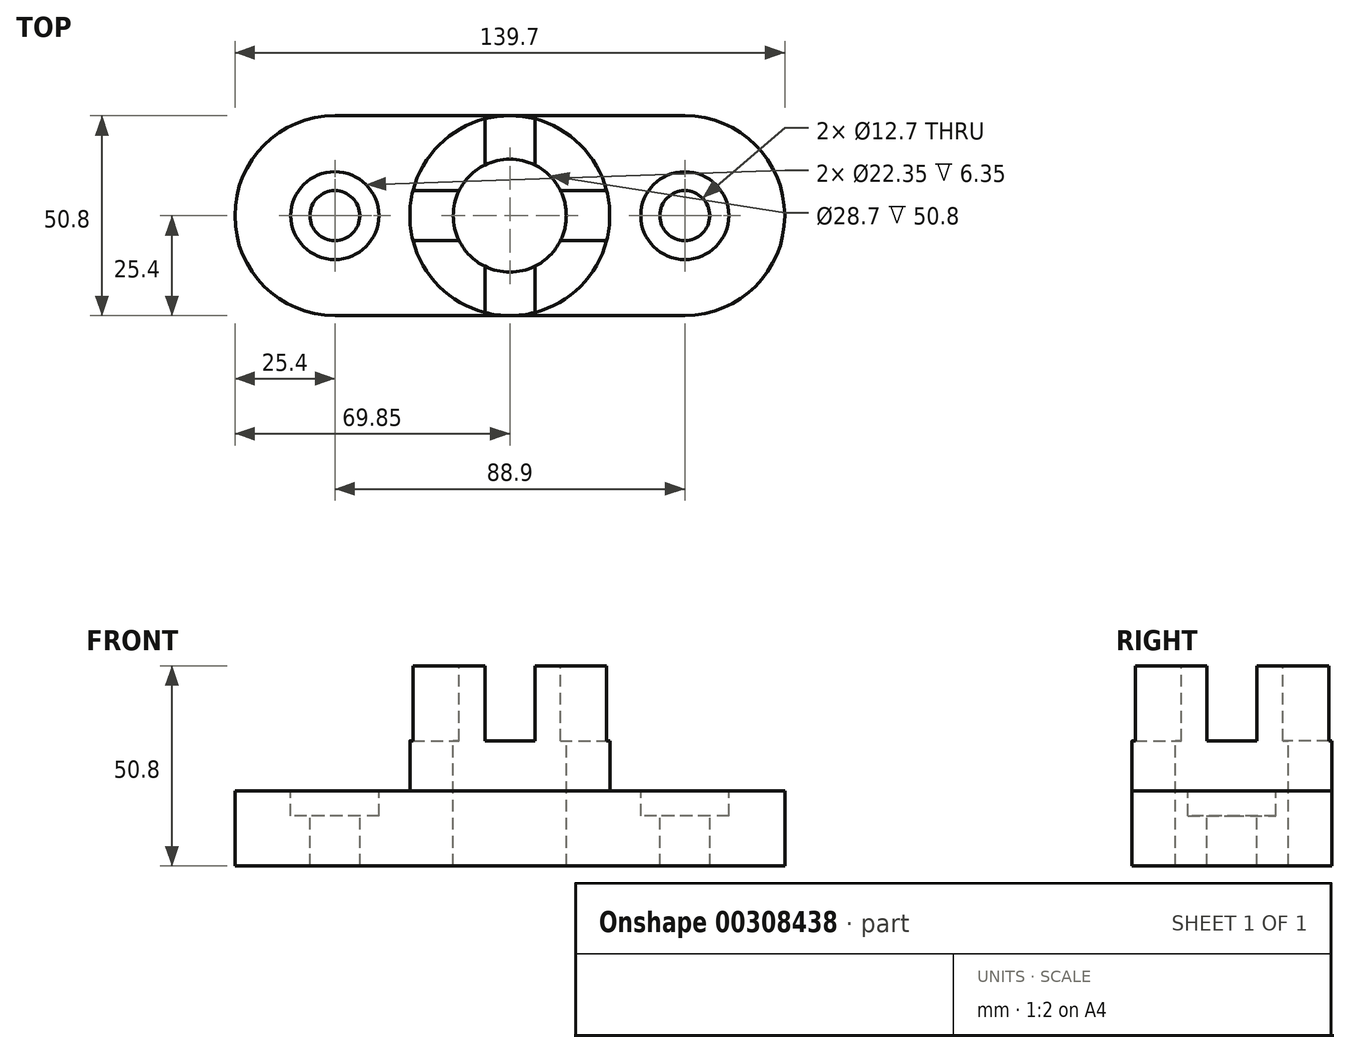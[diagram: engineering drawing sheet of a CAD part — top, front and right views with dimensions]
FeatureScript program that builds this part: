
annotation { "Feature Type Name" : "Feature", "Feature Type Description" : "" }
export const myFeature = defineFeature(function(context is Context, id is Id, definition is map)
    precondition{}
    {
        {
            var Q0;
            Q0=qCreatedBy(makeId("Top.planeOp"),FACE);
            var sketch = newSketch(context, id + "F0", { "sketchPlane" : qUnion([Q0])});
            skLineSegment(sketch, "E0", {"start": v(-44.45, 0) * mm, "end": v(44.45, 0) * mm});
            skLineSegment(sketch, "E1", {"start": v(-44.45, 0) * mm, "end": v(-44.45, 50.8) * mm, "construction": true});
            skLineSegment(sketch, "E2", {"start": v(0, 0) * mm, "end": v(0, 44.45) * mm, "construction": true});
            skArc(sketch, "E3", {"start": v(-44.45, 50.8) * mm, "mid": v(-69.85, 25.4) * mm, "end": v(-44.45, 0) * mm});
            skLineSegment(sketch, "E4.MirrorCS", {"start": v(44.45, 0) * mm, "end": v(44.45, 50.8) * mm, "construction": true});
            skArc(sketch, "E5.MirrorCS", {"start": v(44.45, 50.8) * mm, "mid": v(69.85, 25.4) * mm, "end": v(44.45, 0) * mm});
            skLineSegment(sketch, "E6", {"start": v(-44.45, 50.8) * mm, "end": v(44.45, 50.8) * mm});
            skSolve(sketch);
        }
        {
            var Q0;
            Q0 = qSketchRegion(id + "F0", true);
            extrude(context, id + "F1", {"entities" : qUnion([Q0]), "depth" : 19.05 * mm});
        }
        {
            var Q0;
            Q0=makeQuery(id+"F1.opExtrude","CAP_FACE",FACE,{"disambiguationData":[OSD([sQuery(id+"F0.wireOp",EDGE,"E0"),sQuery(id+"F0.wireOp",EDGE,"E3"),sQuery(id+"F0.wireOp",EDGE,"E5.MirrorCS"),sQuery(id+"F0.wireOp",EDGE,"E6")])],"isStart":false});
            var sketch = newSketch(context, id + "F2", { "sketchPlane" : qUnion([Q0])});
            skCircle(sketch, "E7", {"center": v(-44.45, 25.4) * mm, "radius": 6.35 * mm});
            skCircle(sketch, "E8", {"center": v(-44.45, 25.4) * mm, "radius": 11.18 * mm});
            skCircle(sketch, "E9", {"center": v(44.45, 25.4) * mm, "radius": 6.35 * mm});
            skCircle(sketch, "E10", {"center": v(44.45, 25.4) * mm, "radius": 11.18 * mm});
            skCircle(sketch, "E11", {"center": v(0, 25.4) * mm, "radius": 25.4 * mm});
            skPoint(sketch, "E11.centerSnap0", {"position": v(0, 50.8) * mm});
            skSolve(sketch);
        }
        {
            var Q0;
            Q0=makeQuery(id+"F2.imprint","IMPRINT",FACE,{"disambiguationData":[TD([[makeQuery(id+"F2.imprint","IMPRINT",EDGE,{"derivedFrom":sQuery(id+"F2.wireOp",EDGE,"E7")}),1.0]])]});
            var Q1;
            Q1=makeQuery(id+"F2.imprint","IMPRINT",FACE,{"disambiguationData":[TD([[makeQuery(id+"F2.imprint","IMPRINT",EDGE,{"derivedFrom":sQuery(id+"F2.wireOp",EDGE,"E9")}),1.0]])]});
            extrude(context, id + "F3", {"entities" : qUnion([Q0, Q1]), "operationType" : NewBodyOperationType.REMOVE, "endBound" : BoundingType.THROUGH_ALL, "oppositeDirection" : true, "depth" : 25.4 * mm});
        }
        {
            var Q0;
            Q0=makeQuery(id+"F2.imprint","IMPRINT",FACE,{"disambiguationData":[TD([[makeQuery(id+"F2.imprint","IMPRINT",EDGE,{"derivedFrom":sQuery(id+"F2.wireOp",EDGE,"E7")}),-1.0]])]});
            var Q1;
            Q1=makeQuery(id+"F2.imprint","IMPRINT",FACE,{"disambiguationData":[TD([[makeQuery(id+"F2.imprint","IMPRINT",EDGE,{"derivedFrom":sQuery(id+"F2.wireOp",EDGE,"E9")}),-1.0]])]});
            extrude(context, id + "F4", {"entities" : qUnion([Q0, Q1]), "operationType" : NewBodyOperationType.REMOVE, "oppositeDirection" : true, "depth" : 6.35 * mm});
        }
        {
            var Q0;
            {var subQ0=sQuery(id+"F2.wireOp",EDGE,"E11");var subQ1=makeQuery(id+"F2.imprint","INTERSECT",VERTEX,{"derivedFrom":[makeQuery(id+"F1.opExtrude","CAP_EDGE",EDGE,{"disambiguationData":[OSD([sQuery(id+"F0.wireOp",EDGE,"E0")])],"isStart":false}),subQ0]});Q0=makeQuery(id+"F2.imprint","IMPRINT",FACE,{"disambiguationData":[TD([[makeQuery(id+"F2.imprint","IMPRINT",EDGE,{"disambiguationData":[TD([[subQ1,1.0]])],"derivedFrom":subQ0}),1.0]])]});}
            extrude(context, id + "F5", {"entities" : qUnion([Q0]), "operationType" : NewBodyOperationType.ADD, "depth" : 31.75 * mm});
        }
        {
            var Q0;
            Q0=makeQuery(id+"F5.opExtrude","CAP_FACE",FACE,{"disambiguationData":[OSD([sQuery(id+"F2.wireOp",EDGE,"E11")])],"isStart":false});
            var sketch = newSketch(context, id + "F6", { "sketchPlane" : qUnion([Q0])});
            skLineSegment(sketch, "E12", {"start": v(0, 0) * mm, "end": v(0, 11.05) * mm, "construction": true});
            skLineSegment(sketch, "E13", {"start": v(-14.35, 25.4) * mm, "end": v(-25.4, 25.4) * mm, "construction": true});
            skLineSegment(sketch, "E14", {"start": v(-6.35, 50) * mm, "end": v(-6.35, 38.27) * mm});
            skLineSegment(sketch, "E15", {"start": v(-24.6, 19.05) * mm, "end": v(-12.87, 19.05) * mm});
            skLineSegment(sketch, "E16.MirrorCS", {"start": v(-24.6, 31.75) * mm, "end": v(-12.87, 31.75) * mm});
            skLineSegment(sketch, "E17.MirrorCS", {"start": v(0, 11.05) * mm, "end": v(0, 0) * mm, "construction": true});
            skLineSegment(sketch, "E18.MirrorCS", {"start": v(-6.35, 0.8) * mm, "end": v(-6.35, 12.53) * mm});
            skLineSegment(sketch, "E19.MirrorCS", {"start": v(6.35, 0.8) * mm, "end": v(6.35, 12.53) * mm});
            skLineSegment(sketch, "E20.trimOffspring", {"start": v(12.87, 31.75) * mm, "end": v(24.6, 31.75) * mm});
            skPoint(sketch, "E21.orphan", {"position": v(0, 50.8) * mm});
            skLineSegment(sketch, "E22.trimOffspring", {"start": v(6.35, 38.27) * mm, "end": v(6.35, 50) * mm});
            skLineSegment(sketch, "E23.trimOffspring", {"start": v(-6.35, 38.27) * mm, "end": v(-6.35, 50) * mm});
            skLineSegment(sketch, "E24.trimOffspring", {"start": v(-6.35, 12.53) * mm, "end": v(-6.35, 0.8) * mm});
            skPoint(sketch, "E25.trimOffspring.start.orphan", {"position": v(0, 25.4) * mm});
            skLineSegment(sketch, "E26.trimOffspring", {"start": v(12.87, 19.05) * mm, "end": v(24.6, 19.05) * mm});
            skCircle(sketch, "E27", {"center": v(0, 25.4) * mm, "radius": 14.35 * mm});
            skSolve(sketch);
        }
        {
            var Q0;
            {var subQ0=sQuery(id+"F6.wireOp",EDGE,"E15");Q0=makeQuery(id+"F6.imprint","IMPRINT",FACE,{"disambiguationData":[TD([[makeQuery(id+"F6.imprint","IMPRINT",EDGE,{"derivedFrom":subQ0}),1.0]])]});}
            var Q1;
            {var subQ0=sQuery(id+"F6.wireOp",EDGE,"E22.trimOffspring");Q1=makeQuery(id+"F6.imprint","IMPRINT",FACE,{"disambiguationData":[TD([[makeQuery(id+"F6.imprint","IMPRINT",EDGE,{"derivedFrom":subQ0}),1.0]])]});}
            var Q2;
            {var subQ0=sQuery(id+"F6.wireOp",EDGE,"E20.trimOffspring");Q2=makeQuery(id+"F6.imprint","IMPRINT",FACE,{"disambiguationData":[TD([[makeQuery(id+"F6.imprint","IMPRINT",EDGE,{"derivedFrom":subQ0}),-1.0]])]});}
            var Q3;
            {var subQ0=sQuery(id+"F6.wireOp",EDGE,"E19.MirrorCS");Q3=makeQuery(id+"F6.imprint","IMPRINT",FACE,{"disambiguationData":[TD([[makeQuery(id+"F6.imprint","IMPRINT",EDGE,{"derivedFrom":subQ0}),1.0]])]});}
            extrude(context, id + "F7", {"entities" : qUnion([Q0, Q1, Q2, Q3]), "operationType" : NewBodyOperationType.REMOVE, "oppositeDirection" : true, "depth" : 19.05 * mm});
        }
        {
            var Q0;
            {var subQ0=sQuery(id+"F6.wireOp",EDGE,"E27");var subQ5=makeQuery(id+"F6.imprint","INTERSECT",VERTEX,{"derivedFrom":[sQuery(id+"F6.wireOp",EDGE,"E20.trimOffspring"),subQ0]});Q0=makeQuery(id+"F6.imprint","IMPRINT",FACE,{"disambiguationData":[TD([[makeQuery(id+"F6.imprint","IMPRINT",EDGE,{"disambiguationData":[TD([[subQ5,-1.0]])],"derivedFrom":subQ0}),1.0]])]});}
            extrude(context, id + "F8", {"entities" : qUnion([Q0]), "operationType" : NewBodyOperationType.REMOVE, "endBound" : BoundingType.THROUGH_ALL, "oppositeDirection" : true, "depth" : 25.4 * mm});
        }
    });
